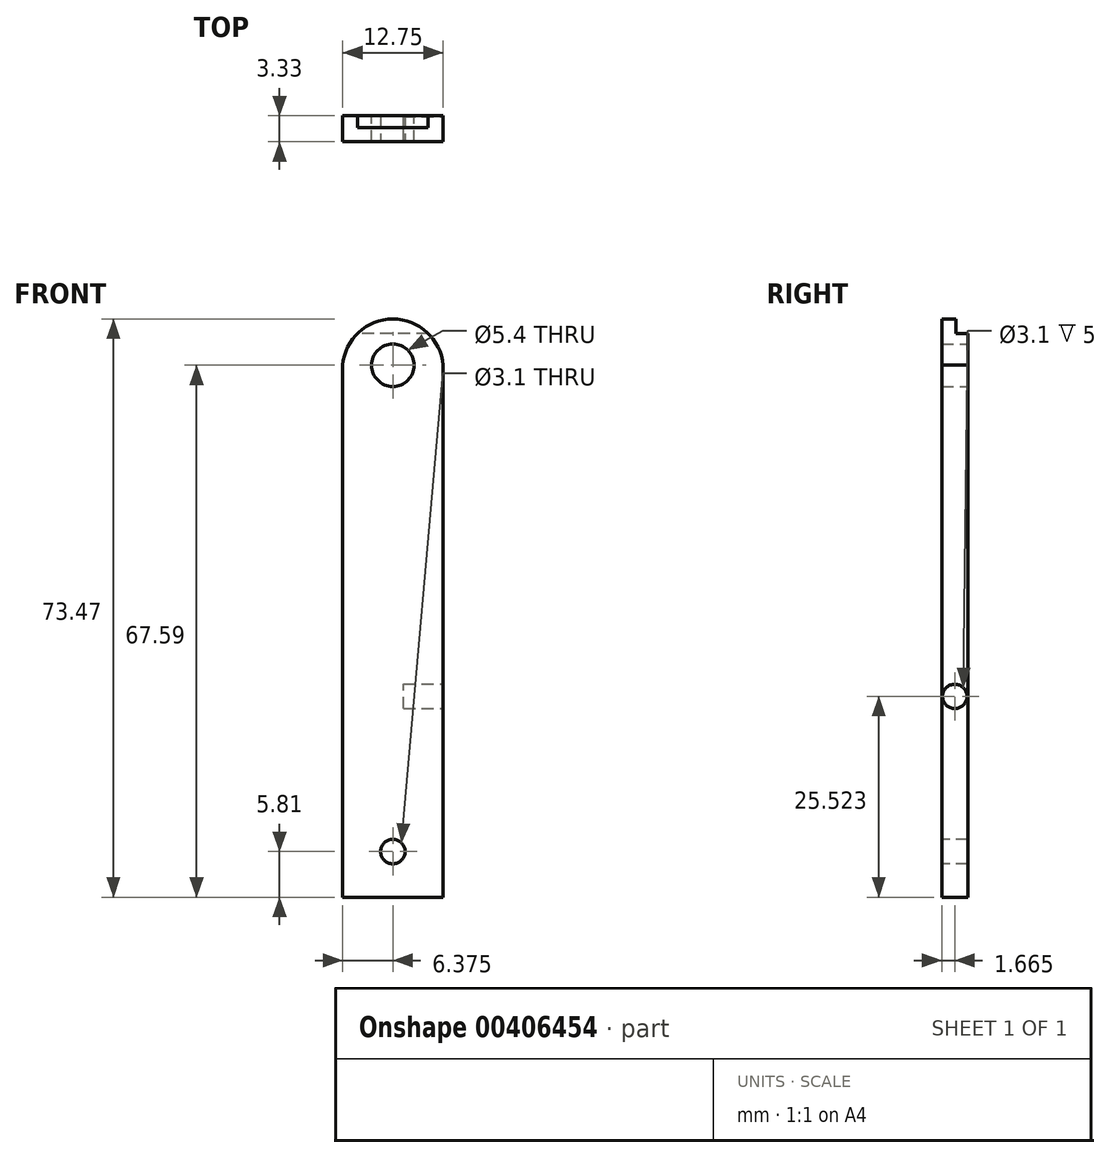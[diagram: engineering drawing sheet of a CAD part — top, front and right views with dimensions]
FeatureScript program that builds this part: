
annotation { "Feature Type Name" : "Feature", "Feature Type Description" : "" }
export const myFeature = defineFeature(function(context is Context, id is Id, definition is map)
    precondition{}
    {
        {
            var Q0;
            Q0=qCreatedBy(makeId("Front.planeOp"),FACE);
            var sketch = newSketch(context, id + "F0", { "sketchPlane" : qUnion([Q0])});
            skLineSegment(sketch, "E0.bottom", {"start": v(0, 0) * mm, "end": v(12.75, 0) * mm});
            skLineSegment(sketch, "E0.top", {"start": v(5.46, 73.4) * mm, "end": v(7.3, 73.4) * mm});
            skLineSegment(sketch, "E0.left", {"start": v(0, 0) * mm, "end": v(0, 67.6) * mm});
            skLineSegment(sketch, "E0.right", {"start": v(12.75, 0) * mm, "end": v(12.75, 67.6) * mm});
            skLineSegment(sketch, "E1", {"start": v(12.75, 67.6) * mm, "end": v(0, 67.6) * mm, "construction": true});
            skCircle(sketch, "E2", {"center": v(6.37, 67.6) * mm, "radius": 2.7 * mm});
            skArc(sketch, "E3", {"start": v(12.75, 67.6) * mm, "mid": v(6.37, 73.47) * mm, "end": v(0, 67.6) * mm});
            skPoint(sketch, "E4.orphan", {"position": v(0, 73.4) * mm});
            skPoint(sketch, "E5.orphan", {"position": v(12.75, 73.4) * mm});
            skSolve(sketch);
        }
        {
            var Q0;
            Q0 = qSketchRegion(id + "F0", true);
            extrude(context, id + "F1", {"entities" : qUnion([Q0]), "depth" : 3.33 * mm});
        }
        {
            var Q0;
            Q0=makeQuery(id+"F1.opExtrude","CAP_FACE",FACE,{"disambiguationData":[OSD([sQuery(id+"F0.wireOp",EDGE,"E0.bottom"),sQuery(id+"F0.wireOp",EDGE,"E0.left"),sQuery(id+"F0.wireOp",EDGE,"E0.right"),sQuery(id+"F0.wireOp",EDGE,"E2"),sQuery(id+"F0.wireOp",EDGE,"E3")])],"isStart":true});
            var sketch = newSketch(context, id + "F2", { "sketchPlane" : qUnion([Q0])});
            skLineSegment(sketch, "E6", {"start": v(-6.37, 73.47) * mm, "end": v(-6.37, 71.67) * mm, "construction": true});
            skLineSegment(sketch, "E7", {"start": v(-6.37, 71.67) * mm, "end": v(-6.37, 72.28) * mm, "construction": true});
            skSolve(sketch);
        }
        {
            var Q0;
            Q0=makeQuery(id+"F2.imprint","IMPRINT",FACE,{"disambiguationData":[TD([[makeQuery(id+"F2.imprint","IMPRINT",EDGE,{"derivedFrom":makeQuery(id+"F1.opExtrude","CAP_EDGE",EDGE,{"disambiguationData":[OSD([sQuery(id+"F0.wireOp",EDGE,"E0.bottom")])],"isStart":true})}),-1.0]])]});
            var sketch = newSketch(context, id + "F3", { "sketchPlane" : qUnion([Q0])});
            skLineSegment(sketch, "E8.bottom", {"start": v(-14.55, 74.88) * mm, "end": v(1.83, 74.88) * mm});
            skLineSegment(sketch, "E8.top", {"start": v(-14.55, 71.63) * mm, "end": v(1.83, 71.63) * mm});
            skLineSegment(sketch, "E8.left", {"start": v(-14.55, 74.88) * mm, "end": v(-14.55, 71.63) * mm});
            skLineSegment(sketch, "E8.right", {"start": v(1.83, 74.88) * mm, "end": v(1.83, 71.63) * mm});
            skSolve(sketch);
        }
        {
            var Q0;
            Q0 = qSketchRegion(id + "F3", true);
            extrude(context, id + "F4", {"entities" : qUnion([Q0]), "operationType" : NewBodyOperationType.REMOVE, "oppositeDirection" : true, "depth" : 1.52 * mm});
        }
        {
            var Q0;
            Q0=makeQuery(id+"F1.opExtrude","CAP_FACE",FACE,{"disambiguationData":[OSD([sQuery(id+"F0.wireOp",EDGE,"E0.bottom"),sQuery(id+"F0.wireOp",EDGE,"E0.left"),sQuery(id+"F0.wireOp",EDGE,"E0.right"),sQuery(id+"F0.wireOp",EDGE,"E2"),sQuery(id+"F0.wireOp",EDGE,"E3")])],"isStart":false});
            var sketch = newSketch(context, id + "F5", { "sketchPlane" : qUnion([Q0])});
            skCircle(sketch, "E9", {"center": v(6.38, 5.8) * mm, "radius": 1.55 * mm});
            skSolve(sketch);
        }
        {
            var Q0;
            Q0 = qSketchRegion(id + "F5", true);
            extrude(context, id + "F6", {"entities" : qUnion([Q0]), "operationType" : NewBodyOperationType.REMOVE, "endBound" : BoundingType.THROUGH_ALL, "oppositeDirection" : true, "depth" : 25 * mm});
        }
        {
            var Q0;
            Q0=makeQuery(id+"F1.opExtrude","SWEPT_FACE",FACE,{"disambiguationData":[OSD([sQuery(id+"F0.wireOp",EDGE,"E0.right")])]});
            var sketch = newSketch(context, id + "F7", { "sketchPlane" : qUnion([Q0])});
            skCircle(sketch, "E10", {"center": v(-1.67, 25.52) * mm, "radius": 1.55 * mm});
            skSolve(sketch);
        }
        {
            var Q0;
            Q0 = qSketchRegion(id + "F7", true);
            extrude(context, id + "F8", {"entities" : qUnion([Q0]), "operationType" : NewBodyOperationType.REMOVE, "oppositeDirection" : true, "depth" : 5 * mm});
        }
    });
